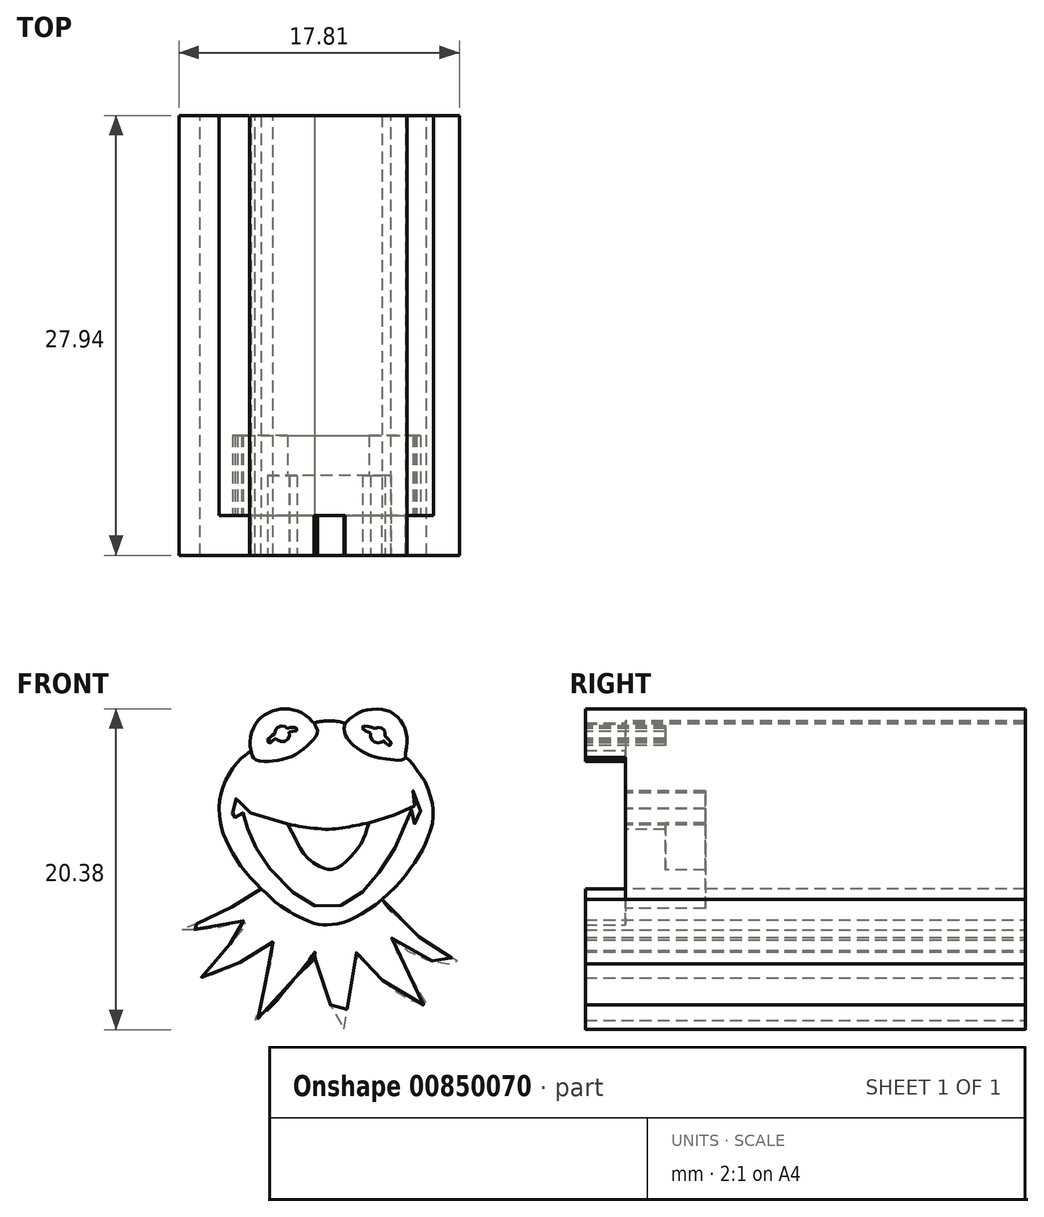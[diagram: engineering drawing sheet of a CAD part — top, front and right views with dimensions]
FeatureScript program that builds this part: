
annotation { "Feature Type Name" : "Feature", "Feature Type Description" : "" }
export const myFeature = defineFeature(function(context is Context, id is Id, definition is map)
    precondition{}
    {
        {
            var Q0;
            Q0=qCreatedBy(makeId("Front.planeOp"),FACE);
            var sketch = newSketch(context, id + "F0", { "sketchPlane" : qUnion([Q0])});
            skLineSegment(sketch, "E0", {"start": v(0, 0) * mm, "end": v(0, 25.4) * mm});
            skLineSegment(sketch, "E1", {"start": v(25.4, 25.4) * mm, "end": v(25.4, 0) * mm});
            skLineSegment(sketch, "E2", {"start": v(25.4, 0) * mm, "end": v(0, 0) * mm});
            skLineSegment(sketch, "E3", {"start": v(25.4, 25.4) * mm, "end": v(0, 25.4) * mm});
            skSolve(sketch);
        }
        {
            var Q0;
            Q0 = qSketchRegion(id + "F0", true);
            extrude(context, id + "F1", {"entities" : qUnion([Q0]), "depth" : 25.4 * mm, "offsetDistance" : 25.4 * mm});
        }
        {
            var Q0;
            Q0=makeQuery(id+"F1.opExtrude","CAP_FACE",FACE,{"disambiguationData":[OSD([sQuery(id+"F0.wireOp",EDGE,"E0"),sQuery(id+"F0.wireOp",EDGE,"E1"),sQuery(id+"F0.wireOp",EDGE,"E2"),sQuery(id+"F0.wireOp",EDGE,"E3")])],"isStart":false});
            var sketch = newSketch(context, id + "F2", { "sketchPlane" : qUnion([Q0])});
            skFitSpline(sketch, "E4", {"points": [v(13.25, 9.2) * mm, v(12.83, 9.2) * mm, v(12.37, 9.28) * mm, v(11.74, 9.52) * mm, v(10.99, 9.88) * mm, v(10.67, 10.09) * mm, v(9.96, 10.56) * mm, v(9.23, 11.2) * mm, v(8.54, 11.9) * mm, v(7.8, 12.72) * mm, v(7.21, 13.61) * mm, v(6.74, 14.48) * mm, v(6.45, 15.22) * mm, v(6.34, 15.74) * mm, v(6.25, 16.8) * mm, v(6.43, 17.71) * mm, v(6.76, 18.52) * mm, v(7.18, 19.24) * mm, v(7.76, 19.85) * mm, v(8.27, 20.27) * mm, v(8.24, 20.44) * mm, v(8.24, 21.07) * mm, v(8.56, 21.93) * mm, v(9.04, 22.46) * mm, v(9.74, 22.81) * mm, v(10.4, 22.92) * mm, v(11.19, 22.8) * mm, v(11.91, 22.39) * mm, v(12.3, 22.02) * mm, v(12.4, 22.05) * mm, v(12.79, 22.13) * mm, v(13.4, 22.15) * mm, v(14.19, 22) * mm, v(14.27, 21.97) * mm, v(14.4, 22.14) * mm, v(14.83, 22.47) * mm, v(15.19, 22.7) * mm, v(15.68, 22.86) * mm, v(16.49, 22.9) * mm, v(17, 22.78) * mm, v(17.52, 22.47) * mm, v(17.96, 21.92) * mm, v(18.15, 21.35) * mm, v(18.2, 20.6) * mm, v(18.11, 19.85) * mm, v(18.37, 19.64) * mm, v(18.86, 18.96) * mm, v(19.33, 18.3) * mm, v(19.73, 17.17) * mm, v(19.86, 16.5) * mm, v(19.8, 15.67) * mm, v(19.55, 14.82) * mm, v(19.18, 13.97) * mm, v(18.65, 13.13) * mm, v(18, 12.24) * mm, v(17.23, 11.39) * mm, v(16.09, 10.4) * mm, v(14.83, 9.63) * mm, v(14, 9.3) * mm, v(13.25, 9.2) * mm]});
            skFitSpline(sketch, "E5", {"points": [v(8.27, 20.27) * mm, v(8.35, 19.99) * mm, v(8.5, 19.73) * mm, v(9.13, 19.59) * mm, v(9.96, 19.64) * mm, v(10.98, 19.95) * mm, v(11.7, 20.43) * mm, v(12.25, 20.95) * mm, v(12.5, 21.44) * mm, v(12.3, 22.02) * mm], "startDerivative": vector(1.02, -3.74) * mm, "endDerivative": vector(-2.96, 5.42) * mm});
            skFitSpline(sketch, "E6", {"points": [v(14.27, 21.97) * mm, v(14.2, 21.72) * mm, v(14.27, 21.26) * mm, v(14.5, 20.94) * mm, v(14.87, 20.55) * mm, v(15.5, 20.13) * mm, v(16.12, 19.86) * mm, v(16.73, 19.74) * mm, v(17.38, 19.68) * mm, v(17.9, 19.68) * mm, v(18.11, 19.85) * mm], "startDerivative": vector(-1.5, -3.07) * mm, "endDerivative": vector(2.48, 2.77) * mm});
            skFitSpline(sketch, "E7", {"points": [v(9.79, 21.34) * mm, v(9.7, 21.29) * mm, v(9.52, 21.14) * mm, v(9.35, 20.96) * mm, v(9.35, 20.84) * mm, v(9.4, 20.77) * mm, v(9.5, 20.76) * mm, v(9.62, 20.86) * mm, v(9.87, 21.04) * mm, v(9.91, 21) * mm, v(10.07, 20.87) * mm, v(10.32, 20.85) * mm, v(10.47, 20.86) * mm, v(10.66, 21.04) * mm, v(10.73, 21.24) * mm, v(10.7, 21.45) * mm, v(10.83, 21.49) * mm, v(11.15, 21.5) * mm, v(11.2, 21.58) * mm, v(11.2, 21.65) * mm, v(11.15, 21.72) * mm, v(10.98, 21.74) * mm, v(10.76, 21.72) * mm, v(10.58, 21.69) * mm, v(10.53, 21.75) * mm, v(10.33, 21.82) * mm, v(10.14, 21.82) * mm, v(9.93, 21.7) * mm, v(9.83, 21.57) * mm, v(9.79, 21.34) * mm]});
            skFitSpline(sketch, "E8", {"points": [v(15.87, 21.39) * mm, v(15.88, 21.1) * mm, v(16.03, 20.89) * mm, v(16.22, 20.79) * mm, v(16.57, 20.8) * mm, v(16.68, 20.9) * mm, v(16.8, 20.8) * mm, v(17, 20.58) * mm, v(17.15, 20.62) * mm, v(17.18, 20.72) * mm, v(17.1, 20.9) * mm, v(16.83, 21.15) * mm, v(16.8, 21.28) * mm, v(16.8, 21.49) * mm, v(16.59, 21.7) * mm, v(16.4, 21.75) * mm, v(16.1, 21.67) * mm, v(16, 21.72) * mm, v(15.61, 21.83) * mm, v(15.42, 21.8) * mm, v(15.4, 21.6) * mm, v(15.87, 21.39) * mm]});
            skFitSpline(sketch, "E9", {"points": [v(8.94, 11.5) * mm, v(8.35, 11.15) * mm, v(7.9, 10.85) * mm, v(7.3, 10.5) * mm, v(6.62, 10.07) * mm, v(5.93, 9.75) * mm, v(5.06, 9.35) * mm, v(4.26, 9.04) * mm, v(3.71, 8.93) * mm, v(3.8, 8.9) * mm, v(4.63, 8.9) * mm, v(5.53, 8.97) * mm, v(6.62, 9.13) * mm, v(8.2, 9.52) * mm, v(8.16, 9.44) * mm, v(7.63, 8.8) * mm, v(6.94, 7.97) * mm, v(6.24, 7.15) * mm, v(5.06, 5.85) * mm, v(5.14, 5.88) * mm, v(5.65, 5.95) * mm, v(6.77, 6.41) * mm, v(7.73, 6.89) * mm, v(8.78, 7.5) * mm, v(9.68, 8.24) * mm, v(9.68, 8.15) * mm, v(9.6, 7.14) * mm, v(9.41, 6.4) * mm, v(9.12, 5.15) * mm, v(8.72, 3.74) * mm, v(8.56, 3.14) * mm, v(8.72, 3.24) * mm, v(9.92, 4.4) * mm, v(10.97, 5.7) * mm, v(11.7, 6.56) * mm, v(12.35, 7.47) * mm, v(12.33, 7.33) * mm, v(12.5, 6.59) * mm, v(12.96, 5.01) * mm, v(13.44, 3.89) * mm, v(14.22, 2.54) * mm, v(14.24, 2.71) * mm, v(14.52, 4.57) * mm, v(14.74, 5.76) * mm, v(15.01, 7.56) * mm, v(15.04, 7.5) * mm, v(15.88, 6.5) * mm, v(16.68, 5.62) * mm, v(17.64, 4.88) * mm, v(18.9, 4.2) * mm, v(19.44, 4.13) * mm, v(19.34, 4.36) * mm, v(18.78, 5.3) * mm, v(18.14, 6.38) * mm, v(17.5, 7.67) * mm, v(17.19, 8.4) * mm, v(17.34, 8.23) * mm, v(18.5, 7.4) * mm, v(19.54, 6.97) * mm, v(20.8, 6.72) * mm, v(21.52, 6.8) * mm, v(21.42, 6.88) * mm, v(20.9, 7.16) * mm, v(20.06, 7.65) * mm, v(19.42, 8.04) * mm, v(18.74, 8.6) * mm, v(17.3, 9.98) * mm, v(16.6, 10.8) * mm], "startDerivative": vector(-46.2, -26.03) * mm, "endDerivative": vector(-35.55, 45.34) * mm});
            skFitSpline(sketch, "E10", {"points": [v(7.69, 17.59) * mm, v(7.47, 17.43) * mm, v(7.25, 17.04) * mm, v(7.17, 16.8) * mm, v(7.14, 16.43) * mm, v(7.12, 15.97) * mm, v(7.28, 15.64) * mm, v(7.27, 15.73) * mm, v(7.34, 16.53) * mm, v(7.4, 16.56) * mm, v(7.78, 16.35) * mm, v(7.78, 16.27) * mm, v(7.92, 15.83) * mm, v(8.02, 15.48) * mm, v(8.18, 14.99) * mm, v(8.5, 14.3) * mm, v(8.77, 13.84) * mm, v(9.22, 13.14) * mm, v(10.37, 11.72) * mm, v(11.25, 11.04) * mm, v(12.04, 10.53) * mm, v(13.16, 10.26) * mm, v(14.04, 10.46) * mm, v(14.95, 10.97) * mm, v(15.58, 11.48) * mm, v(16.2, 12.23) * mm, v(16.78, 13.06) * mm, v(17.5, 14.23) * mm, v(17.84, 14.98) * mm, v(18.1, 15.66) * mm, v(18.28, 16.23) * mm, v(18.35, 16.39) * mm, v(18.76, 16.6) * mm, v(18.78, 16.42) * mm, v(18.69, 15.56) * mm, v(18.72, 15.57) * mm, v(18.94, 15.9) * mm, v(19.06, 16.51) * mm, v(18.93, 17.31) * mm, v(18.57, 17.71) * mm, v(18.6, 17.6) * mm, v(18.77, 16.83) * mm, v(18.68, 16.77) * mm, v(18.09, 16.45) * mm, v(17.44, 16.2) * mm, v(16.35, 15.84) * mm, v(15.5, 15.62) * mm, v(14.36, 15.4) * mm, v(13.28, 15.27) * mm, v(12, 15.37) * mm, v(10.6, 15.6) * mm, v(8.57, 16.19) * mm, v(7.42, 16.77) * mm, v(7.45, 16.84) * mm, v(7.5, 17.1) * mm, v(7.69, 17.59) * mm]});
            skFitSpline(sketch, "E11", {"points": [v(10.6, 15.6) * mm, v(10.87, 15.1) * mm, v(11.27, 14.33) * mm, v(11.93, 13.4) * mm, v(12.9, 12.8) * mm, v(13.27, 12.7) * mm, v(13.9, 12.88) * mm, v(14.59, 13.5) * mm, v(15.14, 14.17) * mm, v(15.49, 14.8) * mm, v(15.77, 15.68) * mm], "startDerivative": vector(3.1, -5.6) * mm, "endDerivative": vector(2.42, 8.58) * mm});
            skSolve(sketch);
        }
        {
            var Q0;
            Q0=makeQuery(id+"F2.imprint","IMPRINT",FACE,{"disambiguationData":[TD([[makeQuery(id+"F2.imprint","IMPRINT",EDGE,{"derivedFrom":sQuery(id+"F2.wireOp",EDGE,"E7")}),1.0]])]});
            var Q1;
            Q1=makeQuery(id+"F2.imprint","IMPRINT",FACE,{"disambiguationData":[TD([[makeQuery(id+"F2.imprint","IMPRINT",EDGE,{"derivedFrom":sQuery(id+"F2.wireOp",EDGE,"E8")}),1.0]])]});
            var Q2;
            {var subQ0=sQuery(id+"F2.wireOp",EDGE,"E11");Q2=makeQuery(id+"F2.imprint","IMPRINT",FACE,{"disambiguationData":[TD([[makeQuery(id+"F2.imprint","IMPRINT",EDGE,{"derivedFrom":subQ0}),1.0]])]});}
            extrude(context, id + "F3", {"entities" : qUnion([Q0, Q1, Q2]), "operationType" : NewBodyOperationType.REMOVE, "oppositeDirection" : true, "depth" : 2.54 * mm, "offsetDistance" : 25.4 * mm});
        }
        {
            var Q0;
            {var subQ0=sQuery(id+"F2.wireOp",EDGE,"E9");Q0=makeQuery(id+"F2.imprint","IMPRINT",FACE,{"disambiguationData":[TD([[makeQuery(id+"F2.imprint","IMPRINT",EDGE,{"derivedFrom":subQ0}),1.0]])]});}
            var Q1;
            {var subQ0=sQuery(id+"F2.wireOp",EDGE,"E5");Q1=makeQuery(id+"F2.imprint","IMPRINT",FACE,{"disambiguationData":[TD([[makeQuery(id+"F2.imprint","IMPRINT",EDGE,{"derivedFrom":subQ0}),1.0]])]});}
            var Q2;
            {var subQ0=sQuery(id+"F2.wireOp",EDGE,"E6");Q2=makeQuery(id+"F2.imprint","IMPRINT",FACE,{"disambiguationData":[TD([[makeQuery(id+"F2.imprint","IMPRINT",EDGE,{"derivedFrom":subQ0}),1.0]])]});}
            extrude(context, id + "F4", {"entities" : qUnion([Q0, Q1, Q2]), "operationType" : NewBodyOperationType.ADD, "depth" : 2.54 * mm, "offsetDistance" : 25.4 * mm});
        }
        {
            var Q0;
            {var subQ0=sQuery(id+"F2.wireOp",EDGE,"E11");Q0=makeQuery(id+"F2.imprint","IMPRINT",FACE,{"disambiguationData":[TD([[makeQuery(id+"F2.imprint","IMPRINT",EDGE,{"derivedFrom":subQ0}),-1.0]])]});}
            extrude(context, id + "F5", {"entities" : qUnion([Q0]), "operationType" : NewBodyOperationType.REMOVE, "oppositeDirection" : true, "depth" : 5.08 * mm, "offsetDistance" : 25.4 * mm});
        }
        {
            var Q0;
            {var subQ7=sQuery(id+"F2.wireOp",EDGE,"E9");Q0=makeQuery(id+"F2.imprint","IMPRINT",FACE,{"disambiguationData":[TD([[makeQuery(id+"F2.imprint","IMPRINT",EDGE,{"derivedFrom":subQ7}),-1.0]])]});}
            extrude(context, id + "F6", {"entities" : qUnion([Q0]), "operationType" : NewBodyOperationType.REMOVE, "oppositeDirection" : true, "depth" : 25.4 * mm, "offsetDistance" : 25.4 * mm});
        }
    });
